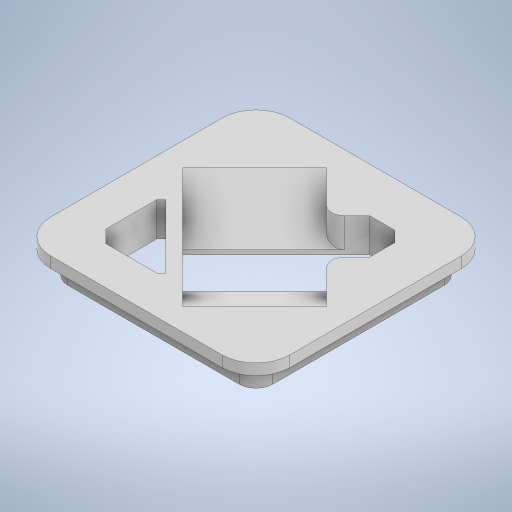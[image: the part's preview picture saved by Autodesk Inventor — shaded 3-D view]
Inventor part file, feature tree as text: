
AUTODESK INVENTOR PART (.ipt)
format: ipt  version: 2024 (Build 280153000, 153)  size: 337,408 bytes
history: native  units: in
note: dims shown in document units (in); Inventor stores cm internally (conversion verified against a paired STEP export)
features: extrude x5, sketch x4, fillet x1
ambient origin geometry x8: Origin, YZ Plane, XZ Plane, XY Plane, X Axis, Y Axis, Z Axis, Center Point
bodies: Body1 (feature_tree)
feature tree (10):
  sketch  "Sketch1"  dims[d0=1.1106in d1=1.1106in]
  extrude  "Extrusion5"  Depth=1.1106in
  extrude  "Extrusion6"  Depth=0.2362in
  extrude  "Extrusion7"  Depth=0.1969in
  extrude  "Extrusion8"  Depth=0.0197in
  extrude  "Extrusion10"  Depth=0.0197in
  fillet  "Fillet2"  Radius=0.1181in
  sketch  "Sketch5"  dims[d2=0.1575in d13=0.2362in]
  sketch  "Sketch6"  dims[d16=0.2362in d18=0.1969in]
  sketch  "Sketch8"  dims[d21=0.0551in d22=0.6142in d24=0.1181in d25=0.1181in d28=0.0787in d29=0.0512in d30=0.0in d31=0.1575in d32=0.0in d33=0.2362in d34=0.0197in d35=0.1575in d36=0.0in d39=0.7874in d43=0.0in d44=0.0in d48=0.0197in d49=0.0197in d50=0.4724in d51=0.0in d52=0.0591in d53=0.4724in d23=0.0197in d42=0.0197in d45=0.0344in d46=0.0344in d47=0.0in d54=0.0in d55=0.0in]
